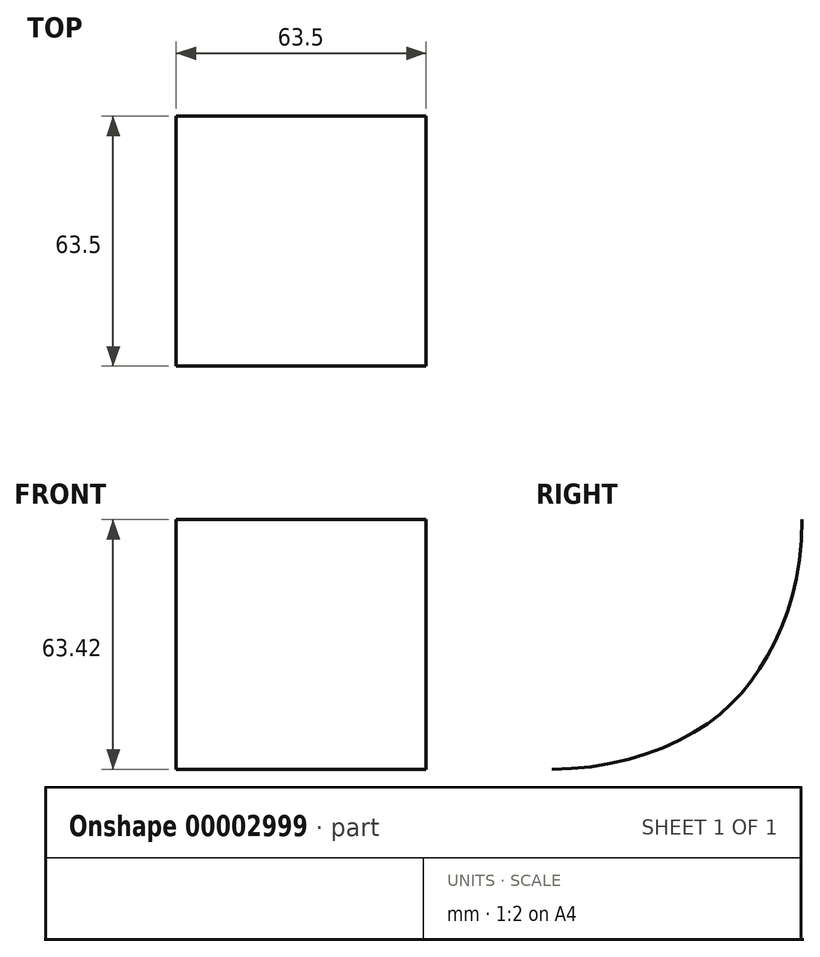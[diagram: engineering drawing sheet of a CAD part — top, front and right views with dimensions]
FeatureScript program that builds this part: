
annotation { "Feature Type Name" : "Feature", "Feature Type Description" : "" }
export const myFeature = defineFeature(function(context is Context, id is Id, definition is map)
    precondition{}
    {
        {
            var Q0;
            Q0=qCreatedBy(makeId("Right.planeOp"),FACE);
            var sketch = newSketch(context, id + "F0", { "sketchPlane" : qUnion([Q0])});
            skFitSpline(sketch, "E0", {"points": [v(0, 63.42) * mm, v(-8.65, 28.99) * mm, v(-26.75, 9.8) * mm, v(-63.5, 0) * mm], "startDerivative": vector(0, -124.1) * mm, "endDerivative": vector(-114.89, 0) * mm});
            skSolve(sketch);
        }
        {
            var Q0;
            Q0=sQuery(id+"F0.wireOp",EDGE,"E0");
            extrude(context, id + "F1", {"bodyType" : ToolBodyType.SURFACE, "surfaceEntities" : qUnion([Q0]), "endBound" : BoundingType.SYMMETRIC, "depth" : 63.5 * mm});
        }
        {
            var Q0;
            Q0=qCreatedBy(makeId("Right.planeOp"),FACE);
            cPlane(context, id + "F2", {"entities" : qUnion([Q0]), "cplaneType" : CPlaneType.OFFSET, "offset" : 31.75 * mm, "width" : 152.4 * mm, "height" : 152.4 * mm});
        }
    });
